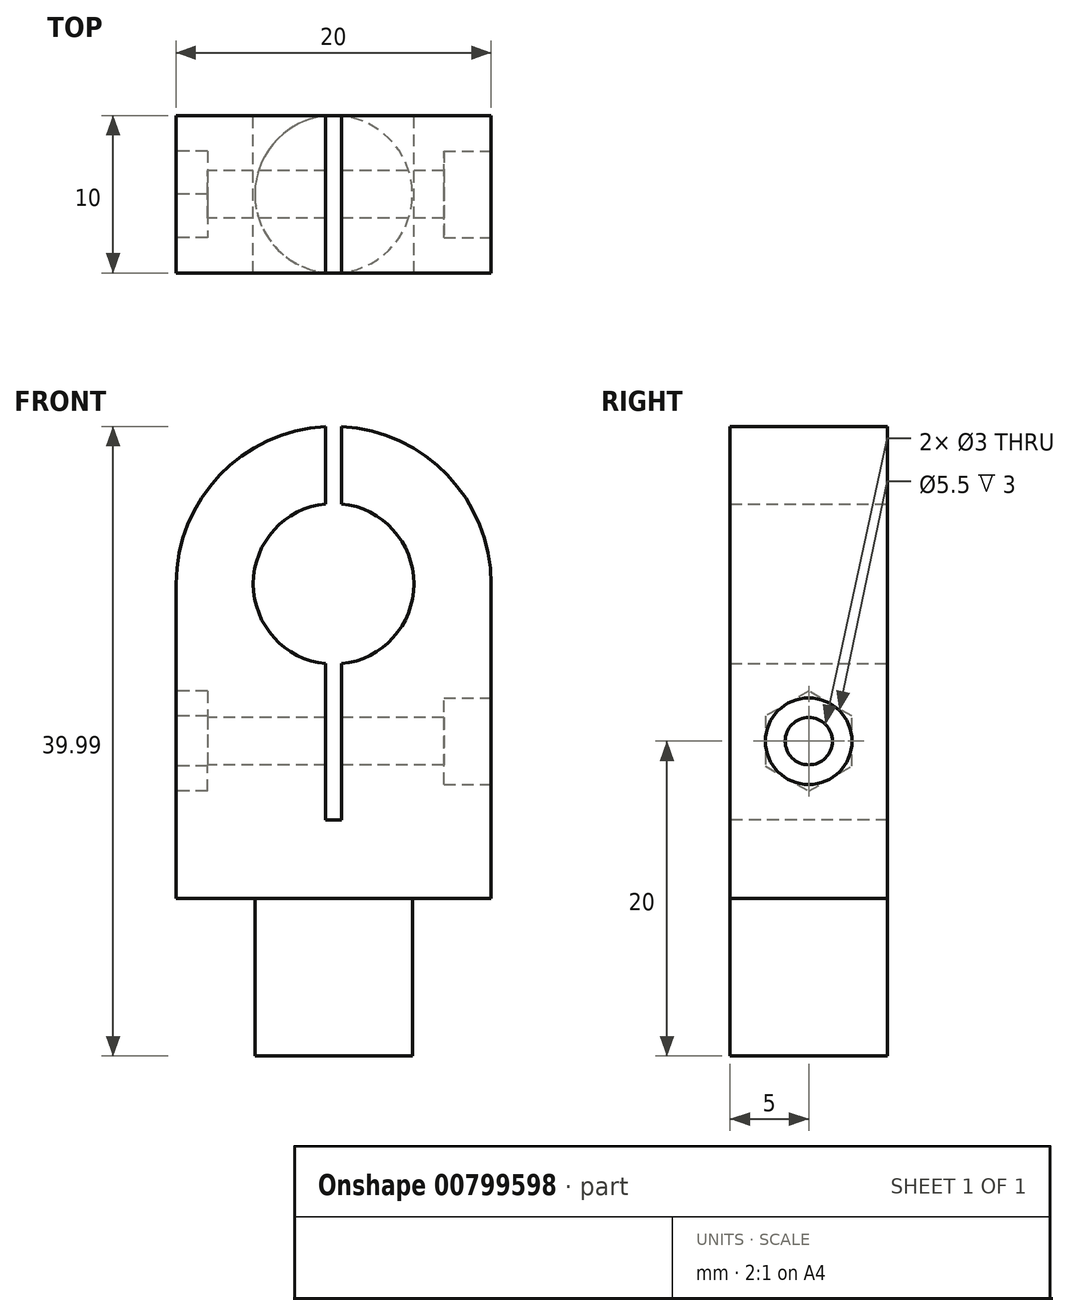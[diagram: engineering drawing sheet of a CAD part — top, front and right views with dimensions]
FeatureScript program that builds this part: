
annotation { "Feature Type Name" : "Feature", "Feature Type Description" : "" }
export const myFeature = defineFeature(function(context is Context, id is Id, definition is map)
    precondition{}
    {
        {
            var Q0;
            Q0=qCreatedBy(makeId("Front.planeOp"),FACE);
            var sketch = newSketch(context, id + "F0", { "sketchPlane" : qUnion([Q0])});
            skCircle(sketch, "E0", {"center": v(0, 0) * mm, "radius": 5.1 * mm});
            skCircle(sketch, "E1", {"center": v(0, 0) * mm, "radius": 10 * mm});
            skLineSegment(sketch, "E2", {"start": v(-10, 0) * mm, "end": v(-10, -20) * mm});
            skLineSegment(sketch, "E3", {"start": v(-10, -20) * mm, "end": v(10, -20) * mm});
            skLineSegment(sketch, "E4", {"start": v(10, -20) * mm, "end": v(10, 0) * mm});
            skSolve(sketch);
        }
        {
            var Q0;
            Q0=makeQuery(id+"F0.imprint","IMPRINT",FACE,{"disambiguationData":[TD([[makeQuery(id+"F0.imprint","IMPRINT",EDGE,{"derivedFrom":sQuery(id+"F0.wireOp",EDGE,"E0")}),-1.0]])]});
            var Q1;
            {var subQ0=sQuery(id+"F0.wireOp",EDGE,"E2");Q1=makeQuery(id+"F0.imprint","IMPRINT",FACE,{"disambiguationData":[TD([[makeQuery(id+"F0.imprint","IMPRINT",EDGE,{"derivedFrom":subQ0}),1.0]])]});}
            extrude(context, id + "F1", {"entities" : qUnion([Q0, Q1]), "depth" : 10 * mm, "offsetDistance" : 25 * mm});
        }
        {
            var Q0;
            Q0=makeQuery(id+"F1.opExtrude","SWEPT_FACE",FACE,{"disambiguationData":[OSD([sQuery(id+"F0.wireOp",EDGE,"E2")])]});
            var sketch = newSketch(context, id + "F2", { "sketchPlane" : qUnion([Q0])});
            skPoint(sketch, "E5", {"position": v(5, -10) * mm});
            skCircle(sketch, "E6", {"center": v(5, -10) * mm, "radius": 1.5 * mm});
            skSolve(sketch);
        }
        {
            var Q0;
            Q0=makeQuery(id+"F2.imprint","IMPRINT",FACE,{"disambiguationData":[TD([[makeQuery(id+"F2.imprint","IMPRINT",EDGE,{"derivedFrom":sQuery(id+"F2.wireOp",EDGE,"E6")}),1.0]])]});
            extrude(context, id + "F3", {"entities" : qUnion([Q0]), "operationType" : NewBodyOperationType.REMOVE, "oppositeDirection" : true, "depth" : 25 * mm, "offsetDistance" : 25 * mm});
        }
        {
            var Q0;
            Q0=makeQuery(id+"F1.opExtrude","CAP_FACE",FACE,{"disambiguationData":[OSD([sQuery(id+"F0.wireOp",EDGE,"E0"),sQuery(id+"F0.wireOp",EDGE,"E1"),sQuery(id+"F0.wireOp",EDGE,"E2"),sQuery(id+"F0.wireOp",EDGE,"E3"),sQuery(id+"F0.wireOp",EDGE,"E4")])],"isStart":false});
            var sketch = newSketch(context, id + "F4", { "sketchPlane" : qUnion([Q0])});
            skLineSegment(sketch, "E7.bottom", {"start": v(-0.5, 12.58) * mm, "end": v(0.5, 12.58) * mm});
            skLineSegment(sketch, "E7.top", {"start": v(-0.5, -15) * mm, "end": v(0.5, -15) * mm});
            skLineSegment(sketch, "E7.left", {"start": v(-0.5, 12.58) * mm, "end": v(-0.5, -15) * mm});
            skLineSegment(sketch, "E7.right", {"start": v(0.5, 12.58) * mm, "end": v(0.5, -15) * mm});
            skSolve(sketch);
        }
        {
            var Q0;
            {var subQ0=sQuery(id+"F4.wireOp",EDGE,"E7.bottom");Q0=makeQuery(id+"F4.imprint","IMPRINT",FACE,{"disambiguationData":[TD([[makeQuery(id+"F4.imprint","IMPRINT",EDGE,{"derivedFrom":subQ0}),-1.0]])]});}
            var Q1;
            {var subQ0=sQuery(id+"F4.wireOp",EDGE,"E7.left");var subQ1=makeQuery(id+"F1.opExtrude","CAP_EDGE",EDGE,{"disambiguationData":[OSD([sQuery(id+"F0.wireOp",EDGE,"E1")])],"isStart":false});var subQ2=makeQuery(id+"F4.imprint","INTERSECT",VERTEX,{"derivedFrom":[subQ1,subQ0]});Q1=makeQuery(id+"F4.imprint","IMPRINT",FACE,{"disambiguationData":[TD([[makeQuery(id+"F4.imprint","IMPRINT",EDGE,{"disambiguationData":[TD([[subQ2,-1.0]])],"derivedFrom":subQ0}),1.0]])]});}
            var Q2;
            {var subQ0=sQuery(id+"F4.wireOp",EDGE,"E7.top");Q2=makeQuery(id+"F4.imprint","IMPRINT",FACE,{"disambiguationData":[TD([[makeQuery(id+"F4.imprint","IMPRINT",EDGE,{"derivedFrom":subQ0}),1.0]])]});}
            var Q3;
            {var subQ0=sQuery(id+"F4.wireOp",EDGE,"E7.left");var subQ1=makeQuery(id+"F1.opExtrude","CAP_EDGE",EDGE,{"disambiguationData":[OSD([sQuery(id+"F0.wireOp",EDGE,"E0")])],"isStart":false});var subQ2=makeQuery(id+"F4.imprint","INTERSECT",VERTEX,{"disambiguationData":[OD(0.0)],"derivedFrom":[subQ1,subQ0]});Q3=makeQuery(id+"F4.imprint","IMPRINT",FACE,{"disambiguationData":[TD([[makeQuery(id+"F4.imprint","IMPRINT",EDGE,{"disambiguationData":[TD([[subQ2,-1.0]])],"derivedFrom":subQ0}),1.0]])]});}
            extrude(context, id + "F5", {"entities" : qUnion([Q0, Q1, Q2, Q3]), "operationType" : NewBodyOperationType.REMOVE, "oppositeDirection" : true, "depth" : 25 * mm, "offsetDistance" : 25 * mm});
        }
        {
            var Q0;
            Q0=makeQuery(id+"F1.opExtrude","SWEPT_FACE",FACE,{"disambiguationData":[OSD([sQuery(id+"F0.wireOp",EDGE,"E3")])]});
            var sketch = newSketch(context, id + "F6", { "sketchPlane" : qUnion([Q0])});
            skPoint(sketch, "E8", {"position": v(0, 5) * mm});
            skCircle(sketch, "E9", {"center": v(0, 5) * mm, "radius": 5 * mm});
            skSolve(sketch);
        }
        {
            var Q0;
            {var subQ0=sQuery(id+"F6.wireOp",EDGE,"E9");var subQ1=sQuery(id+"F0.wireOp",EDGE,"E3");var subQ2=makeQuery(id+"F6.imprint","INTERSECT",VERTEX,{"derivedFrom":[makeQuery(id+"F1.opExtrude","CAP_EDGE",EDGE,{"disambiguationData":[OSD([subQ1])],"isStart":true}),subQ0]});Q0=makeQuery(id+"F6.imprint","IMPRINT",FACE,{"disambiguationData":[TD([[makeQuery(id+"F6.imprint","IMPRINT",EDGE,{"disambiguationData":[TD([[subQ2,1.0]])],"derivedFrom":subQ0}),1.0]])]});}
            extrude(context, id + "F7", {"entities" : qUnion([Q0]), "operationType" : NewBodyOperationType.ADD, "depth" : 10 * mm, "offsetDistance" : 25 * mm});
        }
        {
            var Q0;
            Q0=makeQuery(id+"F1.opExtrude","SWEPT_FACE",FACE,{"disambiguationData":[OSD([sQuery(id+"F0.wireOp",EDGE,"E4")])]});
            var sketch = newSketch(context, id + "F8", { "sketchPlane" : qUnion([Q0])});
            skCircle(sketch, "E10", {"center": v(-5, -10) * mm, "radius": 2.75 * mm});
            skSolve(sketch);
        }
        {
            var Q0;
            Q0=makeQuery(id+"F8.imprint","IMPRINT",FACE,{"disambiguationData":[TD([[makeQuery(id+"F8.imprint","IMPRINT",EDGE,{"derivedFrom":sQuery(id+"F8.wireOp",EDGE,"E10")}),1.0]])]});
            extrude(context, id + "F9", {"entities" : qUnion([Q0]), "operationType" : NewBodyOperationType.REMOVE, "oppositeDirection" : true, "depth" : 3 * mm, "offsetDistance" : 25 * mm});
        }
        {
            var Q0;
            Q0=makeQuery(id+"F1.opExtrude","SWEPT_FACE",FACE,{"disambiguationData":[OSD([sQuery(id+"F0.wireOp",EDGE,"E2")])]});
            var sketch = newSketch(context, id + "F10", { "sketchPlane" : qUnion([Q0])});
            skCircle(sketch, "E11.cCircle", {"center": v(5, -10) * mm, "radius": 2.75 * mm, "construction": true});
            skLineSegment(sketch, "E11.0", {"start": v(7.75, -8.41) * mm, "end": v(7.75, -11.59) * mm});
            skLineSegment(sketch, "E11.1", {"start": v(7.75, -11.59) * mm, "end": v(5, -13.18) * mm});
            skLineSegment(sketch, "E11.2", {"start": v(5, -13.18) * mm, "end": v(2.25, -11.59) * mm});
            skLineSegment(sketch, "E11.3", {"start": v(2.25, -11.59) * mm, "end": v(2.25, -8.41) * mm});
            skLineSegment(sketch, "E11.4", {"start": v(2.25, -8.41) * mm, "end": v(5, -6.82) * mm});
            skLineSegment(sketch, "E11.5", {"start": v(5, -6.82) * mm, "end": v(7.75, -8.41) * mm});
            skPoint(sketch, "E11.0.midPoint", {"position": v(7.75, -10) * mm});
            skSolve(sketch);
        }
        {
            var Q0;
            Q0=makeQuery(id+"F10.imprint","IMPRINT",FACE,{"disambiguationData":[TD([[makeQuery(id+"F10.imprint","IMPRINT",EDGE,{"derivedFrom":sQuery(id+"F10.wireOp",EDGE,"E11.0")}),-1.0]])]});
            extrude(context, id + "F11", {"entities" : qUnion([Q0]), "operationType" : NewBodyOperationType.REMOVE, "oppositeDirection" : true, "depth" : 2 * mm, "offsetDistance" : 25 * mm});
        }
    });
